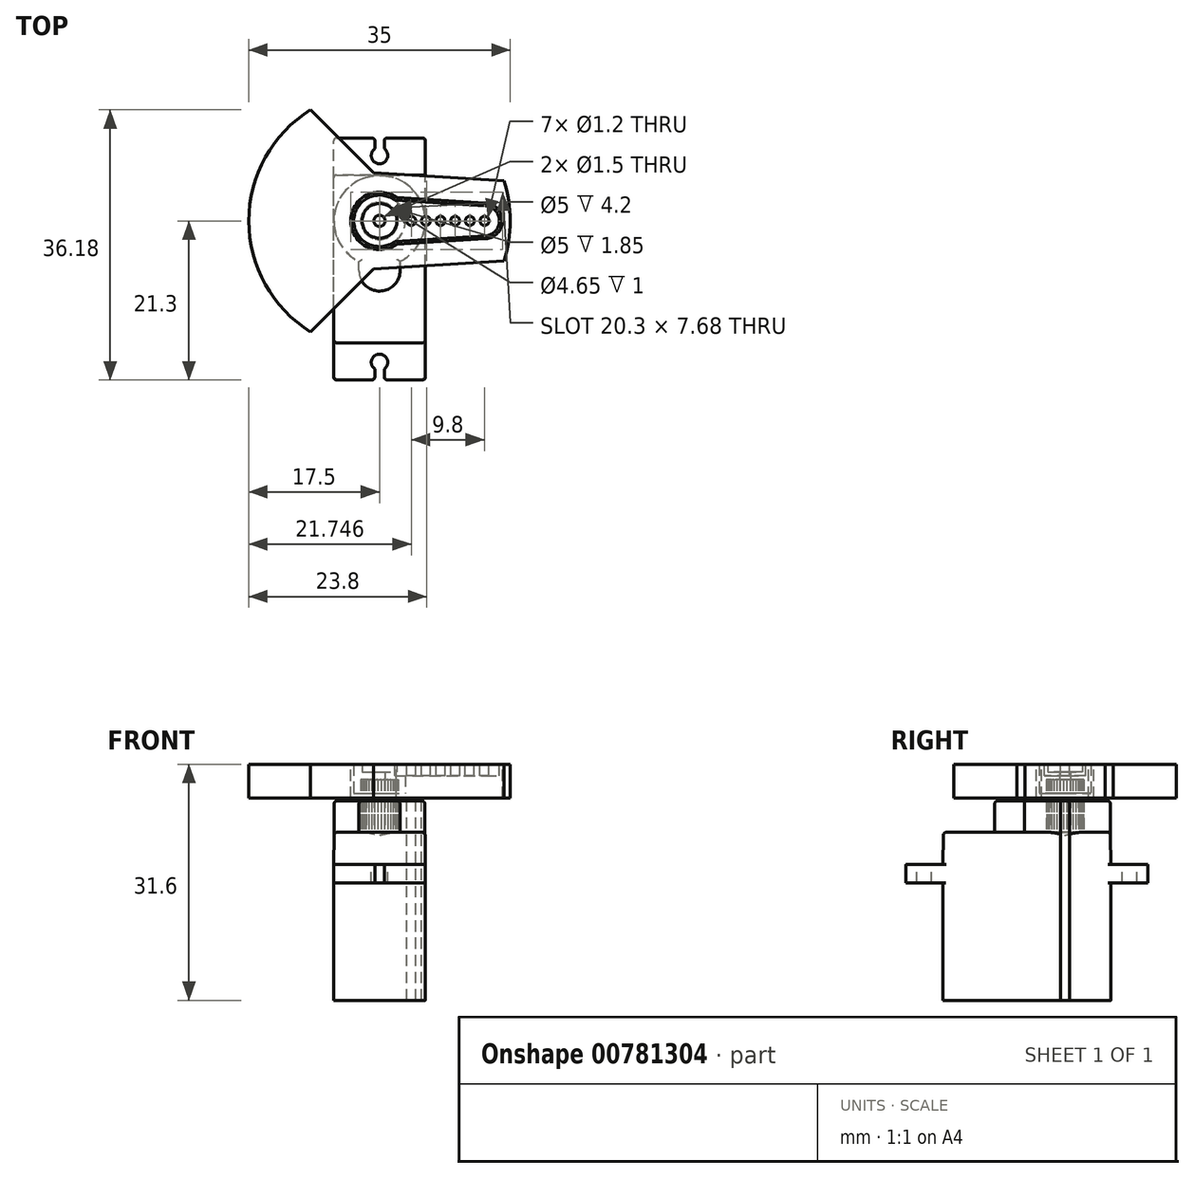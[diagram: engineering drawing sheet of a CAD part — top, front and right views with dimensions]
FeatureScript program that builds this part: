
annotation { "Feature Type Name" : "Feature", "Feature Type Description" : "" }
export const myFeature = defineFeature(function(context is Context, id is Id, definition is map)
    precondition{}
    {
        {
            var Q0;
            Q0=qCreatedBy(makeId("Top.planeOp"),FACE);
            var sketch = newSketch(context, id + "F0", { "sketchPlane" : qUnion([Q0])});
            skLineSegment(sketch, "E0.bottom", {"start": v(6.15, -11.25) * mm, "end": v(-6.15, -11.25) * mm});
            skLineSegment(sketch, "E0.top", {"start": v(6.15, 11.25) * mm, "end": v(-6.15, 11.25) * mm});
            skLineSegment(sketch, "E0.left", {"start": v(6.15, -11.25) * mm, "end": v(6.15, 11.25) * mm});
            skLineSegment(sketch, "E0.right", {"start": v(-6.15, -11.25) * mm, "end": v(-6.15, 11.25) * mm});
            skPoint(sketch, "E0.middle", {"position": v(0, 0) * mm});
            skSolve(sketch);
        }
        {
            var Q0;
            Q0=qSketchRegion(id+"F0",true);
            extrude(context, id + "F1", {"entities" : qUnion([Q0]), "depth" : (22.5 - 15.7) * mm, "hasDraft" : true, "draftAngle" : .5 * degree, "draftPullDirection" : true, "hasSecondDirection" : true, "secondDirectionOppositeDirection" : true, "secondDirectionDepth" : 15.7 * mm});
        }
        {
            var Q0;
            Q0=qCreatedBy(makeId("Top.planeOp"),FACE);
            var sketch = newSketch(context, id + "F2", { "sketchPlane" : qUnion([Q0])});
            skLineSegment(sketch, "E1.bottom", {"start": v(6.15, -16.2) * mm, "end": v(-6.15, -16.2) * mm});
            skLineSegment(sketch, "E1.top", {"start": v(6.15, 16.2) * mm, "end": v(-6.15, 16.2) * mm});
            skLineSegment(sketch, "E1.left", {"start": v(6.15, -16.2) * mm, "end": v(6.15, 16.2) * mm});
            skLineSegment(sketch, "E1.right", {"start": v(-6.15, -16.2) * mm, "end": v(-6.15, 16.2) * mm});
            skPoint(sketch, "E1.middle", {"position": v(0, 0) * mm});
            skSolve(sketch);
        }
        {
            var Q0;
            Q0=qSketchRegion(id+"F2",true);
            extrude(context, id + "F3", {"entities" : qUnion([Q0]), "operationType" : NewBodyOperationType.ADD, "depth" : 2.5 * mm, "hasDraft" : true, "draftAngle" : .5 * degree, "draftPullDirection" : true});
        }
        {
            var Q0;
            {var subQ0=sQuery(id+"F2.wireOp",EDGE,"E1.top");var subQ1=sQuery(id+"F2.wireOp",EDGE,"E1.right");var subQ2=sQuery(id+"F2.wireOp",EDGE,"E1.left");Q0=makeQuery(id+"F3.boolean.opBoolean","SPLIT",FACE,{"disambiguationData":[TD([makeQuery(id+"F1.opExtrude","SWEPT_FACE",FACE,{"disambiguationData":[OSD([sQuery(id+"F0.wireOp",EDGE,"E0.top")])]})])],"derivedFrom":makeQuery(id+"F3.opExtrude","CAP_FACE",FACE,{"disambiguationData":[OSD([sQuery(id+"F2.wireOp",EDGE,"E1.bottom"),subQ0,subQ2,subQ1])],"isStart":false})});}
            var sketch = newSketch(context, id + "F4", { "sketchPlane" : qUnion([Q0])});
            skArc(sketch, "E2", {"start": v(-0.63, 14.76) * mm, "mid": v(0, 12.75) * mm, "end": v(0.63, 14.76) * mm});
            skLineSegment(sketch, "E3", {"start": v(0, 0) * mm, "end": v(0, 13.85) * mm, "construction": true});
            skLineSegment(sketch, "E4", {"start": v(-0.63, 14.76) * mm, "end": v(-0.63, 16.2) * mm});
            skLineSegment(sketch, "E5", {"start": v(-0.62, 16.2) * mm, "end": v(0.62, 16.2) * mm});
            skLineSegment(sketch, "E6", {"start": v(0.62, 16.2) * mm, "end": v(0.62, 14.76) * mm});
            skLineSegment(sketch, "E7", {"start": v(0, 13.85) * mm, "end": v(0, 16.2) * mm, "construction": true});
            skLineSegment(sketch, "E8.MirrorCS", {"start": v(0.62, -16.2) * mm, "end": v(0.62, -14.76) * mm});
            skLineSegment(sketch, "E9.MirrorCS", {"start": v(-0.62, -16.2) * mm, "end": v(0.62, -16.2) * mm});
            skLineSegment(sketch, "E10.MirrorCS", {"start": v(-0.63, -14.76) * mm, "end": v(-0.63, -16.2) * mm});
            skArc(sketch, "E11.MirrorCS", {"start": v(-0.63, -14.76) * mm, "mid": v(0, -12.75) * mm, "end": v(0.63, -14.76) * mm});
            skSolve(sketch);
        }
        {
            var Q0;
            Q0=qSketchRegion(id+"F4",true);
            extrude(context, id + "F5", {"entities" : qUnion([Q0]), "operationType" : NewBodyOperationType.REMOVE, "endBound" : BoundingType.THROUGH_ALL, "oppositeDirection" : true, "depth" : 25 * mm});
        }
        {
            var Q0;
            Q0=makeQuery(id+"F1.*.split.splitOp","SPLIT",EDGE,{"derivedFrom":makeQuery(id+"F1.opExtrude","SWEPT_EDGE",EDGE,{"disambiguationData":[OSD([sQuery(id+"F0.wireOp",EDGE,"E0.bottom"),sQuery(id+"F0.wireOp",EDGE,"E0.left")])]})});
            var Q1;
            Q1=makeQuery(id+"F1.*.split.splitOp","SPLIT",EDGE,{"derivedFrom":makeQuery(id+"F1.opExtrude","SWEPT_EDGE",EDGE,{"disambiguationData":[OSD([sQuery(id+"F0.wireOp",EDGE,"E0.bottom"),sQuery(id+"F0.wireOp",EDGE,"E0.left")])]}),"isFromBackBody":true});
            var Q2;
            Q2=makeQuery(id+"F1.*.split.splitOp","SPLIT",EDGE,{"derivedFrom":makeQuery(id+"F1.opExtrude","SWEPT_EDGE",EDGE,{"disambiguationData":[OSD([sQuery(id+"F0.wireOp",EDGE,"E0.bottom"),sQuery(id+"F0.wireOp",EDGE,"E0.right")])]}),"isFromBackBody":true});
            var Q3;
            Q3=makeQuery(id+"F1.*.split.splitOp","SPLIT",EDGE,{"derivedFrom":makeQuery(id+"F1.opExtrude","SWEPT_EDGE",EDGE,{"disambiguationData":[OSD([sQuery(id+"F0.wireOp",EDGE,"E0.bottom"),sQuery(id+"F0.wireOp",EDGE,"E0.right")])]})});
            var Q4;
            Q4=makeQuery(id+"F1.opExtrude","CAP_FACE",FACE,{"disambiguationData":[OSD([sQuery(id+"F0.wireOp",EDGE,"E0.bottom"),sQuery(id+"F0.wireOp",EDGE,"E0.top"),sQuery(id+"F0.wireOp",EDGE,"E0.left"),sQuery(id+"F0.wireOp",EDGE,"E0.right")])],"isStart":false});
            var Q5;
            Q5=makeQuery(id+"F1.*.split.splitOp","SPLIT",EDGE,{"derivedFrom":makeQuery(id+"F1.opExtrude","SWEPT_EDGE",EDGE,{"disambiguationData":[OSD([sQuery(id+"F0.wireOp",EDGE,"E0.top"),sQuery(id+"F0.wireOp",EDGE,"E0.right")])]})});
            var Q6;
            Q6=makeQuery(id+"F1.*.split.splitOp","SPLIT",EDGE,{"derivedFrom":makeQuery(id+"F1.opExtrude","SWEPT_EDGE",EDGE,{"disambiguationData":[OSD([sQuery(id+"F0.wireOp",EDGE,"E0.top"),sQuery(id+"F0.wireOp",EDGE,"E0.right")])]}),"isFromBackBody":true});
            var Q7;
            Q7=makeQuery(id+"F1.*.split.splitOp","SPLIT",EDGE,{"derivedFrom":makeQuery(id+"F1.opExtrude","SWEPT_EDGE",EDGE,{"disambiguationData":[OSD([sQuery(id+"F0.wireOp",EDGE,"E0.top"),sQuery(id+"F0.wireOp",EDGE,"E0.left")])]}),"isFromBackBody":true});
            var Q8;
            Q8=makeQuery(id+"F1.*.split.splitOp","SPLIT",EDGE,{"derivedFrom":makeQuery(id+"F1.opExtrude","SWEPT_EDGE",EDGE,{"disambiguationData":[OSD([sQuery(id+"F0.wireOp",EDGE,"E0.top"),sQuery(id+"F0.wireOp",EDGE,"E0.left")])]})});
            var Q9;
            Q9=makeQuery(id+"F3.opExtrude","SWEPT_EDGE",EDGE,{"disambiguationData":[OSD([sQuery(id+"F2.wireOp",EDGE,"E1.top"),sQuery(id+"F2.wireOp",EDGE,"E1.left")])]});
            var Q10;
            Q10=makeQuery(id+"F5.boolean.opBoolean","INTERSECT",EDGE,{"derivedFrom":[makeQuery(id+"F3.opExtrude","SWEPT_FACE",FACE,{"disambiguationData":[OSD([sQuery(id+"F2.wireOp",EDGE,"E1.top")])]}),makeQuery(id+"F5.opExtrude","SWEPT_FACE",FACE,{"disambiguationData":[OSD([sQuery(id+"F4.wireOp",EDGE,"E6")])]})]});
            var Q11;
            Q11=makeQuery(id+"F5.boolean.opBoolean","INTERSECT",EDGE,{"derivedFrom":[makeQuery(id+"F3.opExtrude","SWEPT_FACE",FACE,{"disambiguationData":[OSD([sQuery(id+"F2.wireOp",EDGE,"E1.top")])]}),makeQuery(id+"F5.opExtrude","SWEPT_FACE",FACE,{"disambiguationData":[OSD([sQuery(id+"F4.wireOp",EDGE,"E4")])]})]});
            var Q12;
            Q12=makeQuery(id+"F3.opExtrude","SWEPT_EDGE",EDGE,{"disambiguationData":[OSD([sQuery(id+"F2.wireOp",EDGE,"E1.top"),sQuery(id+"F2.wireOp",EDGE,"E1.right")])]});
            var Q13;
            Q13=makeQuery(id+"F3.opExtrude","SWEPT_EDGE",EDGE,{"disambiguationData":[OSD([sQuery(id+"F2.wireOp",EDGE,"E1.bottom"),sQuery(id+"F2.wireOp",EDGE,"E1.right")])]});
            var Q14;
            Q14=makeQuery(id+"F5.boolean.opBoolean","INTERSECT",EDGE,{"derivedFrom":[makeQuery(id+"F3.opExtrude","SWEPT_FACE",FACE,{"disambiguationData":[OSD([sQuery(id+"F2.wireOp",EDGE,"E1.bottom")])]}),makeQuery(id+"F5.opExtrude","SWEPT_FACE",FACE,{"disambiguationData":[OSD([sQuery(id+"F4.wireOp",EDGE,"E10.MirrorCS")])]})]});
            var Q15;
            Q15=makeQuery(id+"F5.boolean.opBoolean","INTERSECT",EDGE,{"derivedFrom":[makeQuery(id+"F3.opExtrude","SWEPT_FACE",FACE,{"disambiguationData":[OSD([sQuery(id+"F2.wireOp",EDGE,"E1.bottom")])]}),makeQuery(id+"F5.opExtrude","SWEPT_FACE",FACE,{"disambiguationData":[OSD([sQuery(id+"F4.wireOp",EDGE,"E8.MirrorCS")])]})]});
            var Q16;
            Q16=makeQuery(id+"F3.opExtrude","SWEPT_EDGE",EDGE,{"disambiguationData":[OSD([sQuery(id+"F2.wireOp",EDGE,"E1.bottom"),sQuery(id+"F2.wireOp",EDGE,"E1.left")])]});
            fillet(context, id + "F6", {"entities" : qUnion([Q0, Q1, Q2, Q3, Q4, Q5, Q6, Q7, Q8, Q9, Q10, Q11, Q12, Q13, Q14, Q15, Q16]), "radius" : .4 * mm, "tangentPropagation" : true, "allowEdgeOverflow" : false});
        }
        {
            var Q0;
            Q0=makeQuery(id+"F1.opExtrude","CAP_FACE",FACE,{"disambiguationData":[OSD([sQuery(id+"F0.wireOp",EDGE,"E0.bottom"),sQuery(id+"F0.wireOp",EDGE,"E0.top"),sQuery(id+"F0.wireOp",EDGE,"E0.left"),sQuery(id+"F0.wireOp",EDGE,"E0.right")])],"isStart":false});
            var sketch = newSketch(context, id + "F7", { "sketchPlane" : qUnion([Q0])});
            skArc(sketch, "E12", {"start": v(2.75, -0.34) * mm, "mid": v(0, 11.2) * mm, "end": v(-2.75, -0.34) * mm});
            skLineSegment(sketch, "E13", {"start": v(-2.75, -0.34) * mm, "end": v(-2.75, -1.56) * mm});
            skLineSegment(sketch, "E14", {"start": v(2.75, -0.34) * mm, "end": v(2.75, -1.56) * mm});
            skArc(sketch, "E15", {"start": v(-2.75, -1.56) * mm, "mid": v(0, -4.3) * mm, "end": v(2.75, -1.56) * mm});
            skCircle(sketch, "E16", {"center": v(0, 5.1) * mm, "radius": 2.5 * mm});
            skSolve(sketch);
        }
        {
            var Q0;
            Q0=qSketchRegion(id+"F7",true);
            extrude(context, id + "F8", {"entities" : qUnion([Q0]), "operationType" : NewBodyOperationType.ADD, "depth" : 4.2 * mm, "hasSecondDirection" : true, "secondDirectionBound" : SecondDirectionBoundingType.UP_TO_NEXT, "secondDirectionOppositeDirection" : true, "secondDirectionDepth" : 25 * mm});
        }
        {
            var Q0;
            Q0=makeQuery(id+"F8.opExtrude","CAP_EDGE",EDGE,{"disambiguationData":[OSD([sQuery(id+"F7.wireOp",EDGE,"E12")])],"isStart":false});
            var Q1;
            Q1=makeQuery(id+"F8.opExtrude","CAP_EDGE",EDGE,{"disambiguationData":[OSD([sQuery(id+"F7.wireOp",EDGE,"E14")])],"isStart":false});
            var Q2;
            Q2=makeQuery(id+"F8.opExtrude","CAP_EDGE",EDGE,{"disambiguationData":[OSD([sQuery(id+"F7.wireOp",EDGE,"E15")])],"isStart":false});
            var Q3;
            Q3=makeQuery(id+"F8.opExtrude","CAP_EDGE",EDGE,{"disambiguationData":[OSD([sQuery(id+"F7.wireOp",EDGE,"E13")])],"isStart":false});
            fillet(context, id + "F9", {"entities" : qUnion([Q0, Q1, Q2, Q3]), "radius" : .4 * mm, "tangentPropagation" : true, "allowEdgeOverflow" : false});
        }
        {
            var Q0;
            Q0=makeQuery(id+"F8.opExtrude","CAP_FACE",FACE,{"disambiguationData":[OSD([sQuery(id+"F7.wireOp",EDGE,"E12"),sQuery(id+"F7.wireOp",EDGE,"E13"),sQuery(id+"F7.wireOp",EDGE,"E14"),sQuery(id+"F7.wireOp",EDGE,"E15"),sQuery(id+"F7.wireOp",EDGE,"E16")])],"isStart":false});
            var sketch = newSketch(context, id + "F10", { "sketchPlane" : qUnion([Q0])});
            skCircle(sketch, "E17", {"center": v(0, 5.1) * mm, "radius": 2.3 * mm, "construction": true});
            skLineSegment(sketch, "E18", {"start": v(-0.23, 7.39) * mm, "end": v(-0.06, 7.57) * mm});
            skLineSegment(sketch, "E19", {"start": v(0.23, 7.39) * mm, "end": v(0.06, 7.57) * mm});
            skArc(sketch, "E20", {"start": v(0.06, 7.57) * mm, "mid": v(0, 7.6) * mm, "end": v(-0.06, 7.57) * mm});
            skLineSegment(sketch, "E21", {"start": v(-0.23, 7.39) * mm, "end": v(0, 5.1) * mm, "construction": true});
            skLineSegment(sketch, "E22", {"start": v(0.23, 7.39) * mm, "end": v(0, 5.1) * mm, "construction": true});
            skLineSegment(sketch, "E23.1.0", {"start": v(-0.67, 7.3) * mm, "end": v(-0.54, 7.51) * mm});
            skArc(sketch, "E23.1.1", {"start": v(-0.42, 7.54) * mm, "mid": v(-0.49, 7.55) * mm, "end": v(-0.54, 7.51) * mm});
            skLineSegment(sketch, "E23.1.2", {"start": v(-0.23, 7.39) * mm, "end": v(-0.42, 7.54) * mm});
            skLineSegment(sketch, "E23.2.0", {"start": v(-1.08, 7.13) * mm, "end": v(-1, 7.36) * mm});
            skArc(sketch, "E23.2.1", {"start": v(-0.9, 7.4) * mm, "mid": v(-0.96, 7.4) * mm, "end": v(-1, 7.36) * mm});
            skLineSegment(sketch, "E23.2.2", {"start": v(-0.67, 7.3) * mm, "end": v(-0.9, 7.4) * mm});
            skLineSegment(sketch, "E23.3.0", {"start": v(-1.46, 6.88) * mm, "end": v(-1.42, 7.12) * mm});
            skArc(sketch, "E23.3.1", {"start": v(-1.32, 7.19) * mm, "mid": v(-1.39, 7.18) * mm, "end": v(-1.42, 7.12) * mm});
            skLineSegment(sketch, "E23.3.2", {"start": v(-1.08, 7.13) * mm, "end": v(-1.32, 7.19) * mm});
            skLineSegment(sketch, "E23.4.0", {"start": v(-1.78, 6.56) * mm, "end": v(-1.8, 6.8) * mm});
            skArc(sketch, "E23.4.1", {"start": v(-1.7, 6.9) * mm, "mid": v(-1.77, 6.87) * mm, "end": v(-1.8, 6.8) * mm});
            skLineSegment(sketch, "E23.4.2", {"start": v(-1.46, 6.88) * mm, "end": v(-1.7, 6.9) * mm});
            skLineSegment(sketch, "E23.5.0", {"start": v(-2.03, 6.18) * mm, "end": v(-2.09, 6.42) * mm});
            skArc(sketch, "E23.5.1", {"start": v(-2.02, 6.52) * mm, "mid": v(-2.08, 6.49) * mm, "end": v(-2.09, 6.42) * mm});
            skLineSegment(sketch, "E23.5.2", {"start": v(-1.78, 6.56) * mm, "end": v(-2.02, 6.52) * mm});
            skLineSegment(sketch, "E23.6.0", {"start": v(-2.2, 5.77) * mm, "end": v(-2.3, 6) * mm});
            skArc(sketch, "E23.6.1", {"start": v(-2.26, 6.1) * mm, "mid": v(-2.3, 6.06) * mm, "end": v(-2.3, 6) * mm});
            skLineSegment(sketch, "E23.6.2", {"start": v(-2.03, 6.18) * mm, "end": v(-2.26, 6.1) * mm});
            skLineSegment(sketch, "E23.7.0", {"start": v(-2.29, 5.33) * mm, "end": v(-2.44, 5.52) * mm});
            skArc(sketch, "E23.7.1", {"start": v(-2.41, 5.64) * mm, "mid": v(-2.45, 5.59) * mm, "end": v(-2.44, 5.52) * mm});
            skLineSegment(sketch, "E23.7.2", {"start": v(-2.2, 5.77) * mm, "end": v(-2.41, 5.64) * mm});
            skLineSegment(sketch, "E23.8.0", {"start": v(-2.29, 4.87) * mm, "end": v(-2.47, 5.04) * mm});
            skArc(sketch, "E23.8.1", {"start": v(-2.47, 5.16) * mm, "mid": v(-2.5, 5.1) * mm, "end": v(-2.47, 5.04) * mm});
            skLineSegment(sketch, "E23.8.2", {"start": v(-2.29, 5.33) * mm, "end": v(-2.47, 5.16) * mm});
            skLineSegment(sketch, "E23.9.0", {"start": v(-2.2, 4.43) * mm, "end": v(-2.41, 4.56) * mm});
            skArc(sketch, "E23.9.1", {"start": v(-2.44, 4.68) * mm, "mid": v(-2.45, 4.61) * mm, "end": v(-2.41, 4.56) * mm});
            skLineSegment(sketch, "E23.9.2", {"start": v(-2.29, 4.87) * mm, "end": v(-2.44, 4.68) * mm});
            skLineSegment(sketch, "E23.10.0", {"start": v(-2.03, 4.02) * mm, "end": v(-2.26, 4.1) * mm});
            skArc(sketch, "E23.10.1", {"start": v(-2.3, 4.2) * mm, "mid": v(-2.3, 4.14) * mm, "end": v(-2.26, 4.1) * mm});
            skLineSegment(sketch, "E23.10.2", {"start": v(-2.2, 4.43) * mm, "end": v(-2.3, 4.2) * mm});
            skLineSegment(sketch, "E23.11.0", {"start": v(-1.78, 3.64) * mm, "end": v(-2.02, 3.68) * mm});
            skArc(sketch, "E23.11.1", {"start": v(-2.09, 3.78) * mm, "mid": v(-2.08, 3.71) * mm, "end": v(-2.02, 3.68) * mm});
            skLineSegment(sketch, "E23.11.2", {"start": v(-2.03, 4.02) * mm, "end": v(-2.09, 3.78) * mm});
            skLineSegment(sketch, "E23.12.0", {"start": v(-1.46, 3.32) * mm, "end": v(-1.7, 3.3) * mm});
            skArc(sketch, "E23.12.1", {"start": v(-1.8, 3.4) * mm, "mid": v(-1.77, 3.33) * mm, "end": v(-1.7, 3.3) * mm});
            skLineSegment(sketch, "E23.12.2", {"start": v(-1.78, 3.64) * mm, "end": v(-1.8, 3.4) * mm});
            skLineSegment(sketch, "E23.13.0", {"start": v(-1.08, 3.07) * mm, "end": v(-1.32, 3.01) * mm});
            skArc(sketch, "E23.13.1", {"start": v(-1.42, 3.08) * mm, "mid": v(-1.39, 3.02) * mm, "end": v(-1.32, 3.01) * mm});
            skLineSegment(sketch, "E23.13.2", {"start": v(-1.46, 3.32) * mm, "end": v(-1.42, 3.08) * mm});
            skLineSegment(sketch, "E23.14.0", {"start": v(-0.67, 2.9) * mm, "end": v(-0.9, 2.8) * mm});
            skArc(sketch, "E23.14.1", {"start": v(-1, 2.84) * mm, "mid": v(-0.96, 2.8) * mm, "end": v(-0.9, 2.8) * mm});
            skLineSegment(sketch, "E23.14.2", {"start": v(-1.08, 3.07) * mm, "end": v(-1, 2.84) * mm});
            skLineSegment(sketch, "E23.15.0", {"start": v(-0.23, 2.81) * mm, "end": v(-0.42, 2.66) * mm});
            skArc(sketch, "E23.15.1", {"start": v(-0.54, 2.69) * mm, "mid": v(-0.49, 2.65) * mm, "end": v(-0.42, 2.66) * mm});
            skLineSegment(sketch, "E23.15.2", {"start": v(-0.67, 2.9) * mm, "end": v(-0.54, 2.69) * mm});
            skLineSegment(sketch, "E23.16.0", {"start": v(0.23, 2.81) * mm, "end": v(0.06, 2.63) * mm});
            skArc(sketch, "E23.16.1", {"start": v(-0.06, 2.63) * mm, "mid": v(0, 2.6) * mm, "end": v(0.06, 2.63) * mm});
            skLineSegment(sketch, "E23.16.2", {"start": v(-0.23, 2.81) * mm, "end": v(-0.06, 2.63) * mm});
            skLineSegment(sketch, "E23.17.0", {"start": v(0.67, 2.9) * mm, "end": v(0.54, 2.69) * mm});
            skArc(sketch, "E23.17.1", {"start": v(0.42, 2.66) * mm, "mid": v(0.49, 2.65) * mm, "end": v(0.54, 2.69) * mm});
            skLineSegment(sketch, "E23.17.2", {"start": v(0.23, 2.81) * mm, "end": v(0.42, 2.66) * mm});
            skLineSegment(sketch, "E23.18.0", {"start": v(1.08, 3.07) * mm, "end": v(1, 2.84) * mm});
            skArc(sketch, "E23.18.1", {"start": v(0.9, 2.8) * mm, "mid": v(0.96, 2.8) * mm, "end": v(1, 2.84) * mm});
            skLineSegment(sketch, "E23.18.2", {"start": v(0.67, 2.9) * mm, "end": v(0.9, 2.8) * mm});
            skLineSegment(sketch, "E23.19.0", {"start": v(1.46, 3.32) * mm, "end": v(1.42, 3.08) * mm});
            skArc(sketch, "E23.19.1", {"start": v(1.32, 3.01) * mm, "mid": v(1.39, 3.02) * mm, "end": v(1.42, 3.08) * mm});
            skLineSegment(sketch, "E23.19.2", {"start": v(1.08, 3.07) * mm, "end": v(1.32, 3.01) * mm});
            skLineSegment(sketch, "E23.20.0", {"start": v(1.78, 3.64) * mm, "end": v(1.8, 3.4) * mm});
            skArc(sketch, "E23.20.1", {"start": v(1.7, 3.3) * mm, "mid": v(1.77, 3.33) * mm, "end": v(1.8, 3.4) * mm});
            skLineSegment(sketch, "E23.20.2", {"start": v(1.46, 3.32) * mm, "end": v(1.7, 3.3) * mm});
            skLineSegment(sketch, "E23.21.0", {"start": v(2.03, 4.02) * mm, "end": v(2.09, 3.78) * mm});
            skArc(sketch, "E23.21.1", {"start": v(2.02, 3.68) * mm, "mid": v(2.08, 3.71) * mm, "end": v(2.09, 3.78) * mm});
            skLineSegment(sketch, "E23.21.2", {"start": v(1.78, 3.64) * mm, "end": v(2.02, 3.68) * mm});
            skLineSegment(sketch, "E23.22.0", {"start": v(2.2, 4.43) * mm, "end": v(2.3, 4.2) * mm});
            skArc(sketch, "E23.22.1", {"start": v(2.26, 4.1) * mm, "mid": v(2.3, 4.14) * mm, "end": v(2.3, 4.2) * mm});
            skLineSegment(sketch, "E23.22.2", {"start": v(2.03, 4.02) * mm, "end": v(2.26, 4.1) * mm});
            skLineSegment(sketch, "E23.23.0", {"start": v(2.29, 4.87) * mm, "end": v(2.44, 4.68) * mm});
            skArc(sketch, "E23.23.1", {"start": v(2.41, 4.56) * mm, "mid": v(2.45, 4.61) * mm, "end": v(2.44, 4.68) * mm});
            skLineSegment(sketch, "E23.23.2", {"start": v(2.2, 4.43) * mm, "end": v(2.41, 4.56) * mm});
            skLineSegment(sketch, "E23.24.0", {"start": v(2.29, 5.33) * mm, "end": v(2.47, 5.16) * mm});
            skArc(sketch, "E23.24.1", {"start": v(2.47, 5.04) * mm, "mid": v(2.5, 5.1) * mm, "end": v(2.47, 5.16) * mm});
            skLineSegment(sketch, "E23.24.2", {"start": v(2.29, 4.87) * mm, "end": v(2.47, 5.04) * mm});
            skLineSegment(sketch, "E23.25.0", {"start": v(2.2, 5.77) * mm, "end": v(2.41, 5.64) * mm});
            skArc(sketch, "E23.25.1", {"start": v(2.44, 5.52) * mm, "mid": v(2.45, 5.59) * mm, "end": v(2.41, 5.64) * mm});
            skLineSegment(sketch, "E23.25.2", {"start": v(2.29, 5.33) * mm, "end": v(2.44, 5.52) * mm});
            skLineSegment(sketch, "E23.26.0", {"start": v(2.03, 6.18) * mm, "end": v(2.26, 6.1) * mm});
            skArc(sketch, "E23.26.1", {"start": v(2.3, 6) * mm, "mid": v(2.3, 6.06) * mm, "end": v(2.26, 6.1) * mm});
            skLineSegment(sketch, "E23.26.2", {"start": v(2.2, 5.77) * mm, "end": v(2.3, 6) * mm});
            skLineSegment(sketch, "E23.27.0", {"start": v(1.78, 6.56) * mm, "end": v(2.02, 6.52) * mm});
            skArc(sketch, "E23.27.1", {"start": v(2.09, 6.42) * mm, "mid": v(2.08, 6.49) * mm, "end": v(2.02, 6.52) * mm});
            skLineSegment(sketch, "E23.27.2", {"start": v(2.03, 6.18) * mm, "end": v(2.09, 6.42) * mm});
            skLineSegment(sketch, "E23.28.0", {"start": v(1.46, 6.88) * mm, "end": v(1.7, 6.9) * mm});
            skArc(sketch, "E23.28.1", {"start": v(1.8, 6.8) * mm, "mid": v(1.77, 6.87) * mm, "end": v(1.7, 6.9) * mm});
            skLineSegment(sketch, "E23.28.2", {"start": v(1.78, 6.56) * mm, "end": v(1.8, 6.8) * mm});
            skLineSegment(sketch, "E23.29.0", {"start": v(1.08, 7.13) * mm, "end": v(1.32, 7.19) * mm});
            skArc(sketch, "E23.29.1", {"start": v(1.42, 7.12) * mm, "mid": v(1.39, 7.18) * mm, "end": v(1.32, 7.19) * mm});
            skLineSegment(sketch, "E23.29.2", {"start": v(1.46, 6.88) * mm, "end": v(1.42, 7.12) * mm});
            skLineSegment(sketch, "E23.30.0", {"start": v(0.67, 7.3) * mm, "end": v(0.9, 7.4) * mm});
            skArc(sketch, "E23.30.1", {"start": v(1, 7.36) * mm, "mid": v(0.96, 7.4) * mm, "end": v(0.9, 7.4) * mm});
            skLineSegment(sketch, "E23.30.2", {"start": v(1.08, 7.13) * mm, "end": v(1, 7.36) * mm});
            skLineSegment(sketch, "E23.31.0", {"start": v(0.23, 7.39) * mm, "end": v(0.42, 7.54) * mm});
            skArc(sketch, "E23.31.1", {"start": v(0.54, 7.51) * mm, "mid": v(0.49, 7.55) * mm, "end": v(0.42, 7.54) * mm});
            skLineSegment(sketch, "E23.31.2", {"start": v(0.67, 7.3) * mm, "end": v(0.54, 7.51) * mm});
            skCircle(sketch, "E24", {"center": v(0, 5.1) * mm, "radius": 0.75 * mm});
            skSolve(sketch);
        }
        {
            var Q0;
            Q0=qSketchRegion(id+"F10",true);
            extrude(context, id + "F11", {"entities" : qUnion([Q0]), "depth" : 2.85 * mm, "hasSecondDirection" : true, "secondDirectionBound" : SecondDirectionBoundingType.UP_TO_NEXT, "secondDirectionOppositeDirection" : true, "secondDirectionDepth" : 25 * mm, "offsetDistance" : 25 * mm});
        }
        {
            var Q0;
            Q0=qCreatedBy(makeId("Right.planeOp"),FACE);
            var sketch = newSketch(context, id + "F12", { "sketchPlane" : qUnion([Q0])});
            skLineSegment(sketch, "E25.0", {"start": v(4.35, 13.85) * mm, "end": v(5.85, 13.85) * mm, "construction": true});
            skLineSegment(sketch, "E26", {"start": v(5.85, 13.85) * mm, "end": v(7.6, 13.85) * mm});
            skLineSegment(sketch, "E27", {"start": v(7.6, 13.85) * mm, "end": v(7.6, 12) * mm});
            skLineSegment(sketch, "E28", {"start": v(7.6, 12) * mm, "end": v(8.55, 12) * mm});
            skLineSegment(sketch, "E29", {"start": v(8.55, 12) * mm, "end": v(8.55, 15.9) * mm});
            skLineSegment(sketch, "E30", {"start": v(8.55, 15.9) * mm, "end": v(7.43, 15.9) * mm});
            skLineSegment(sketch, "E31", {"start": v(7.43, 15.9) * mm, "end": v(7.43, 14.9) * mm});
            skLineSegment(sketch, "E32", {"start": v(7.43, 14.9) * mm, "end": v(5.85, 14.9) * mm});
            skLineSegment(sketch, "E33", {"start": v(5.85, 14.9) * mm, "end": v(5.85, 13.85) * mm});
            skLineSegment(sketch, "E34", {"start": v(5.1, 13.85) * mm, "end": v(5.1, 16.3) * mm, "construction": true});
            skLineSegment(sketch, "E35.0", {"start": v(2.6, 11) * mm, "end": v(7.6, 11) * mm, "construction": true});
            skSolve(sketch);
        }
        {
            var Q0;
            Q0=qSketchRegion(id+"F12",true);
            var Q1;
            Q1=qSketchRegion(id+"F19",true);
            var Q2;
            Q2=sQuery(id+"F12.wireOp",EDGE,"E34");
            revolve(context, id + "F13", {"entities" : qUnion([Q0, Q1]), "axis" : qUnion([Q2]), "revolveType" : RevolveType.FULL, "surfaceOperationType" : NewSurfaceOperationType.NEW});
        }
        {
            var Q0;
            Q0=makeQuery(id+"F13.opRevolve","SWEPT_FACE",FACE,{"disambiguationData":[OSD([sQuery(id+"F12.wireOp",EDGE,"E30")])]});
            var sketch = newSketch(context, id + "F14", { "sketchPlane" : qUnion([Q0])});
            skLineSegment(sketch, "E36", {"start": v(2.08, 2.35) * mm, "end": v(14.17, 3.1) * mm});
            skLineSegment(sketch, "E37", {"start": v(2.08, 7.85) * mm, "end": v(14.17, 7.1) * mm});
            skLineSegment(sketch, "E38", {"start": v(0, 5.1) * mm, "end": v(14.05, 5.1) * mm, "construction": true});
            skArc(sketch, "E39", {"start": v(14.17, 3.1) * mm, "mid": v(16.05, 5.1) * mm, "end": v(14.17, 7.1) * mm});
            skArc(sketch, "E40.0", {"start": v(2.08, 2.35) * mm, "mid": v(3.45, 5.1) * mm, "end": v(2.08, 7.85) * mm});
            skSolve(sketch);
        }
        {
            var Q0;
            Q0=qSketchRegion(id+"F14",true);
            extrude(context, id + "F15", {"entities" : qUnion([Q0]), "operationType" : NewBodyOperationType.ADD, "oppositeDirection" : true, "depth" : 1.5 * mm, "offsetDistance" : 25 * mm});
        }
        {
            var Q0;
            Q0=makeQuery(id+"F15.boolean.opBoolean","MERGE",FACE,{"derivedFrom":[makeQuery(id+"F13.opRevolve","SWEPT_FACE",FACE,{"disambiguationData":[OSD([sQuery(id+"F12.wireOp",EDGE,"E30")])]}),makeQuery(id+"F15.opExtrude","CAP_FACE",FACE,{"disambiguationData":[OSD([sQuery(id+"F14.wireOp",EDGE,"E36"),sQuery(id+"F14.wireOp",EDGE,"E37"),sQuery(id+"F14.wireOp",EDGE,"E39"),sQuery(id+"F14.wireOp",EDGE,"E40.0")])],"isStart":true})]});
            var sketch = newSketch(context, id + "F16", { "sketchPlane" : qUnion([Q0])});
            skCircle(sketch, "E41", {"center": v(14.05, 5.1) * mm, "radius": 0.6 * mm});
            skCircle(sketch, "E42.1.0.0", {"center": v(12.09, 5.1) * mm, "radius": 0.6 * mm});
            skCircle(sketch, "E42.2.0.0", {"center": v(10.13, 5.1) * mm, "radius": 0.6 * mm});
            skCircle(sketch, "E42.3.0.0", {"center": v(8.17, 5.1) * mm, "radius": 0.6 * mm});
            skCircle(sketch, "E42.4.0.0", {"center": v(6.2, 5.1) * mm, "radius": 0.6 * mm});
            skCircle(sketch, "E42.5.0.0", {"center": v(4.25, 5.1) * mm, "radius": 0.6 * mm});
            skLineSegment(sketch, "E42.direction1", {"start": v(14.05, 5.1) * mm, "end": v(12.09, 5.1) * mm, "construction": true});
            skSolve(sketch);
        }
        {
            var Q0;
            Q0=qSketchRegion(id+"F16",true);
            extrude(context, id + "F17", {"entities" : qUnion([Q0]), "operationType" : NewBodyOperationType.REMOVE, "endBound" : BoundingType.THROUGH_ALL, "oppositeDirection" : true, "depth" : 25 * mm, "offsetDistance" : 25 * mm});
        }
        {
            var Q0;
            Q0=makeQuery(id+"F15.boolean.opBoolean","MERGE",FACE,{"derivedFrom":[makeQuery(id+"F13.opRevolve","SWEPT_FACE",FACE,{"disambiguationData":[OSD([sQuery(id+"F12.wireOp",EDGE,"E30")])]}),makeQuery(id+"F15.opExtrude","CAP_FACE",FACE,{"disambiguationData":[OSD([sQuery(id+"F14.wireOp",EDGE,"E36"),sQuery(id+"F14.wireOp",EDGE,"E37"),sQuery(id+"F14.wireOp",EDGE,"E39"),sQuery(id+"F14.wireOp",EDGE,"E40.0")])],"isStart":true})]});
            var sketch = newSketch(context, id + "F18", { "sketchPlane" : qUnion([Q0])});
            skArc(sketch, "E43.0", {"start": v(2.22, 8.24) * mm, "mid": v(-3.85, 5.1) * mm, "end": v(2.22, 1.96) * mm});
            skLineSegment(sketch, "E43.1", {"start": v(14.2, 7.5) * mm, "end": v(2.22, 8.24) * mm});
            skArc(sketch, "E43.2", {"start": v(14.2, 2.7) * mm, "mid": v(16.45, 5.1) * mm, "end": v(14.2, 7.5) * mm});
            skLineSegment(sketch, "E43.3", {"start": v(2.22, 1.96) * mm, "end": v(14.2, 2.7) * mm});
            skSolve(sketch);
        }
        {
            var Q0;
            Q0=makeQuery(id+"F18.imprint","IMPRINT",FACE,{"disambiguationData":[TD([[makeQuery(id+"F18.imprint","IMPRINT",EDGE,{"derivedFrom":sQuery(id+"F18.wireOp",EDGE,"E43.0")}),1.0]])]});
            var sketch = newSketch(context, id + "F19", { "sketchPlane" : qUnion([Q0])});
            skCircle(sketch, "E44", {"center": v(0, 5.1) * mm, "radius": 17.5 * mm});
            skLineSegment(sketch, "E45", {"start": v(0, 5.1) * mm, "end": v(-14.14, -9.04) * mm});
            skLineSegment(sketch, "E46", {"start": v(0, 5.1) * mm, "end": v(-20.07, 5.1) * mm});
            skLineSegment(sketch, "E47.MirrorCS", {"start": v(0, 5.1) * mm, "end": v(-14.14, 19.24) * mm});
            skCircle(sketch, "E48", {"center": v(-14, 5.1) * mm, "radius": 2 * mm});
            skCircle(sketch, "E49", {"center": v(0, 5.1) * mm, "radius": 14 * mm});
            skCircle(sketch, "E50.1.0", {"center": v(-12.93, 10.46) * mm, "radius": 2 * mm});
            skCircle(sketch, "E50.2.0", {"center": v(-9.9, 15) * mm, "radius": 2 * mm});
            skLineSegment(sketch, "E50.anchor1", {"start": v(0, 5.1) * mm, "end": v(-14, 5.1) * mm, "construction": true});
            skLineSegment(sketch, "E50.anchor2", {"start": v(0, 5.1) * mm, "end": v(-9.9, 15) * mm, "construction": true});
            skCircle(sketch, "E51.MirrorC", {"center": v(-12.93, -0.26) * mm, "radius": 2 * mm});
            skCircle(sketch, "E52.MirrorC", {"center": v(-9.9, -4.8) * mm, "radius": 2 * mm});
            skLineSegment(sketch, "E53.0", {"start": v(5.66, 5.1) * mm, "end": v(-11.31, 22.07) * mm});
            skLineSegment(sketch, "E53.1", {"start": v(5.66, 5.1) * mm, "end": v(-11.31, -11.87) * mm});
            skLineSegment(sketch, "E54", {"start": v(0, 5.1) * mm, "end": v(-12.93, -0.26) * mm});
            skLineSegment(sketch, "E55", {"start": v(0, 5.1) * mm, "end": v(-12.93, 10.46) * mm});
            skLineSegment(sketch, "E56", {"start": v(-12.04, 12.25) * mm, "end": v(19.23, 10.3) * mm});
            skLineSegment(sketch, "E57.MirrorCS", {"start": v(-12.04, -2.05) * mm, "end": v(19.23, -0.1) * mm});
            skSolve(sketch);
        }
        {
            var Q0;
            {var subQ5=sQuery(id+"F19.wireOp",EDGE,"E53.0");var subQ7=sQuery(id+"F19.wireOp",EDGE,"E44");var subQ8=makeQuery(id+"F19.imprint","INTERSECT",VERTEX,{"derivedFrom":[subQ7,subQ5]});Q0=makeQuery(id+"F19.imprint","IMPRINT",FACE,{"disambiguationData":[TD([[makeQuery(id+"F19.imprint","IMPRINT",EDGE,{"disambiguationData":[TD([[subQ8,-1.0]])],"derivedFrom":subQ7}),1.0]])]});}
            var Q1;
            {var subQ3=sQuery(id+"F19.wireOp",EDGE,"E56");var subQ6=sQuery(id+"F19.wireOp",EDGE,"E47.MirrorCS");var subQ9=makeQuery(id+"F19.imprint","INTERSECT",VERTEX,{"derivedFrom":[subQ6,subQ3]});Q1=makeQuery(id+"F19.imprint","IMPRINT",FACE,{"disambiguationData":[TD([[makeQuery(id+"F19.imprint","IMPRINT",EDGE,{"disambiguationData":[TD([[subQ9,-1.0]])],"derivedFrom":subQ6}),-1.0]])]});}
            var Q2;
            {var subQ3=sQuery(id+"F19.wireOp",EDGE,"E47.MirrorCS");var subQ5=sQuery(id+"F19.wireOp",EDGE,"E56");var subQ9=makeQuery(id+"F19.imprint","INTERSECT",VERTEX,{"derivedFrom":[subQ3,subQ5]});Q2=makeQuery(id+"F19.imprint","IMPRINT",FACE,{"disambiguationData":[TD([[makeQuery(id+"F19.imprint","IMPRINT",EDGE,{"disambiguationData":[TD([[subQ9,1.0]])],"derivedFrom":subQ3}),-1.0]])]});}
            var Q3;
            {var subQ0=sQuery(id+"F19.wireOp",EDGE,"E56");var subQ1=sQuery(id+"F19.wireOp",EDGE,"E49");var subQ2=makeQuery(id+"F19.imprint","INTERSECT",VERTEX,{"derivedFrom":[subQ1,subQ0]});Q3=makeQuery(id+"F19.imprint","IMPRINT",FACE,{"disambiguationData":[TD([[makeQuery(id+"F19.imprint","IMPRINT",EDGE,{"disambiguationData":[TD([[subQ2,1.0]])],"derivedFrom":subQ1}),1.0]])]});}
            var Q4;
            {var subQ12=makeQuery(id+"F18.imprint","IMPRINT",EDGE,{"derivedFrom":sQuery(id+"F18.wireOp",EDGE,"E43.2")});Q4=makeQuery(id+"F19.imprint","IMPRINT",FACE,{"disambiguationData":[TD([[makeQuery(id+"F19.imprint","IMPRINT",EDGE,{"derivedFrom":subQ12}),-1.0]])]});}
            var Q5;
            {var subQ0=sQuery(id+"F19.wireOp",EDGE,"E57.MirrorCS");var subQ1=sQuery(id+"F19.wireOp",EDGE,"E49");var subQ2=makeQuery(id+"F19.imprint","INTERSECT",VERTEX,{"derivedFrom":[subQ1,subQ0]});Q5=makeQuery(id+"F19.imprint","IMPRINT",FACE,{"disambiguationData":[TD([[makeQuery(id+"F19.imprint","IMPRINT",EDGE,{"disambiguationData":[TD([[subQ2,-1.0]])],"derivedFrom":subQ1}),1.0]])]});}
            var Q6;
            {var subQ3=sQuery(id+"F19.wireOp",EDGE,"E45");var subQ5=sQuery(id+"F19.wireOp",EDGE,"E57.MirrorCS");var subQ9=makeQuery(id+"F19.imprint","INTERSECT",VERTEX,{"derivedFrom":[subQ3,subQ5]});Q6=makeQuery(id+"F19.imprint","IMPRINT",FACE,{"disambiguationData":[TD([[makeQuery(id+"F19.imprint","IMPRINT",EDGE,{"disambiguationData":[TD([[subQ9,1.0]])],"derivedFrom":subQ3}),1.0]])]});}
            var Q7;
            {var subQ0=sQuery(id+"F19.wireOp",EDGE,"E57.MirrorCS");var subQ3=sQuery(id+"F19.wireOp",EDGE,"E45");var subQ4=makeQuery(id+"F19.imprint","INTERSECT",VERTEX,{"derivedFrom":[subQ3,subQ0]});Q7=makeQuery(id+"F19.imprint","IMPRINT",FACE,{"disambiguationData":[TD([[makeQuery(id+"F19.imprint","IMPRINT",EDGE,{"disambiguationData":[TD([[subQ4,1.0]])],"derivedFrom":subQ3}),-1.0]])]});}
            var Q8;
            {var subQ0=sQuery(id+"F19.wireOp",EDGE,"E56");var subQ3=sQuery(id+"F19.wireOp",EDGE,"E47.MirrorCS");var subQ4=makeQuery(id+"F19.imprint","INTERSECT",VERTEX,{"derivedFrom":[subQ3,subQ0]});Q8=makeQuery(id+"F19.imprint","IMPRINT",FACE,{"disambiguationData":[TD([[makeQuery(id+"F19.imprint","IMPRINT",EDGE,{"disambiguationData":[TD([[subQ4,1.0]])],"derivedFrom":subQ3}),1.0]])]});}
            var Q9;
            {var subQ1=sQuery(id+"F19.wireOp",EDGE,"E48");var subQ9=sQuery(id+"F19.wireOp",EDGE,"E46");var subQ10=makeQuery(id+"F19.imprint","INTERSECT",VERTEX,{"disambiguationData":[OD(0.0)],"derivedFrom":[subQ9,subQ1]});Q9=makeQuery(id+"F19.imprint","IMPRINT",FACE,{"disambiguationData":[TD([[makeQuery(id+"F19.imprint","IMPRINT",EDGE,{"disambiguationData":[TD([[subQ10,1.0]])],"derivedFrom":subQ9}),-1.0]])]});}
            var Q10;
            {var subQ5=sQuery(id+"F19.wireOp",EDGE,"E48");var subQ6=sQuery(id+"F19.wireOp",EDGE,"E46");var subQ7=makeQuery(id+"F19.imprint","INTERSECT",VERTEX,{"disambiguationData":[OD(0.0)],"derivedFrom":[subQ6,subQ5]});Q10=makeQuery(id+"F19.imprint","IMPRINT",FACE,{"disambiguationData":[TD([[makeQuery(id+"F19.imprint","IMPRINT",EDGE,{"disambiguationData":[TD([[subQ7,1.0]])],"derivedFrom":subQ6}),1.0]])]});}
            var Q11;
            {var subQ3=sQuery(id+"F19.wireOp",EDGE,"E57.MirrorCS");var subQ5=sQuery(id+"F19.wireOp",EDGE,"E45");var subQ6=makeQuery(id+"F19.imprint","INTERSECT",VERTEX,{"derivedFrom":[subQ5,subQ3]});Q11=makeQuery(id+"F19.imprint","IMPRINT",FACE,{"disambiguationData":[TD([[makeQuery(id+"F19.imprint","IMPRINT",EDGE,{"disambiguationData":[TD([[subQ6,-1.0]])],"derivedFrom":subQ5}),1.0]])]});}
            var Q12;
            {var subQ0=sQuery(id+"F19.wireOp",EDGE,"E57.MirrorCS");var subQ1=sQuery(id+"F19.wireOp",EDGE,"E45");var subQ2=makeQuery(id+"F19.imprint","INTERSECT",VERTEX,{"derivedFrom":[subQ1,subQ0]});Q12=makeQuery(id+"F19.imprint","IMPRINT",FACE,{"disambiguationData":[TD([[makeQuery(id+"F19.imprint","IMPRINT",EDGE,{"disambiguationData":[TD([[subQ2,-1.0]])],"derivedFrom":subQ1}),-1.0]])]});}
            var Q13;
            {var subQ0=sQuery(id+"F19.wireOp",EDGE,"E56");var subQ1=sQuery(id+"F19.wireOp",EDGE,"E47.MirrorCS");var subQ2=makeQuery(id+"F19.imprint","INTERSECT",VERTEX,{"derivedFrom":[subQ1,subQ0]});Q13=makeQuery(id+"F19.imprint","IMPRINT",FACE,{"disambiguationData":[TD([[makeQuery(id+"F19.imprint","IMPRINT",EDGE,{"disambiguationData":[TD([[subQ2,-1.0]])],"derivedFrom":subQ1}),1.0]])]});}
            var Q14;
            {var subQ5=sQuery(id+"F19.wireOp",EDGE,"E47.MirrorCS");var subQ6=sQuery(id+"F19.wireOp",EDGE,"E44");var subQ7=makeQuery(id+"F19.imprint","INTERSECT",VERTEX,{"derivedFrom":[subQ6,subQ5]});Q14=makeQuery(id+"F19.imprint","IMPRINT",FACE,{"disambiguationData":[TD([[makeQuery(id+"F19.imprint","IMPRINT",EDGE,{"disambiguationData":[TD([[subQ7,-1.0]])],"derivedFrom":subQ6}),1.0]])]});}
            var Q15;
            {var subQ1=sQuery(id+"F19.wireOp",EDGE,"E46");var subQ8=sQuery(id+"F19.wireOp",EDGE,"E44");var subQ9=makeQuery(id+"F19.imprint","INTERSECT",VERTEX,{"derivedFrom":[subQ8,subQ1]});Q15=makeQuery(id+"F19.imprint","IMPRINT",FACE,{"disambiguationData":[TD([[makeQuery(id+"F19.imprint","IMPRINT",EDGE,{"disambiguationData":[TD([[subQ9,-1.0]])],"derivedFrom":subQ8}),1.0]])]});}
            var Q16;
            {var subQ1=sQuery(id+"F19.wireOp",EDGE,"E45");var subQ5=sQuery(id+"F19.wireOp",EDGE,"E44");var subQ6=makeQuery(id+"F19.imprint","INTERSECT",VERTEX,{"derivedFrom":[subQ5,subQ1]});Q16=makeQuery(id+"F19.imprint","IMPRINT",FACE,{"disambiguationData":[TD([[makeQuery(id+"F19.imprint","IMPRINT",EDGE,{"disambiguationData":[TD([[subQ6,-1.0]])],"derivedFrom":subQ5}),1.0]])]});}
            var Q17;
            {var subQ0=sQuery(id+"F19.wireOp",EDGE,"E49");var subQ1=sQuery(id+"F19.wireOp",EDGE,"E47.MirrorCS");var subQ2=makeQuery(id+"F19.imprint","INTERSECT",VERTEX,{"derivedFrom":[subQ1,subQ0]});Q17=makeQuery(id+"F19.imprint","IMPRINT",FACE,{"disambiguationData":[TD([[makeQuery(id+"F19.imprint","IMPRINT",EDGE,{"disambiguationData":[TD([[subQ2,-1.0]])],"derivedFrom":subQ1}),-1.0]])]});}
            var Q18;
            {var subQ0=sQuery(id+"F19.wireOp",EDGE,"E49");var subQ1=sQuery(id+"F19.wireOp",EDGE,"E47.MirrorCS");var subQ2=makeQuery(id+"F19.imprint","INTERSECT",VERTEX,{"derivedFrom":[subQ1,subQ0]});Q18=makeQuery(id+"F19.imprint","IMPRINT",FACE,{"disambiguationData":[TD([[makeQuery(id+"F19.imprint","IMPRINT",EDGE,{"disambiguationData":[TD([[subQ2,-1.0]])],"derivedFrom":subQ1}),1.0]])]});}
            var Q19;
            {var subQ0=sQuery(id+"F19.wireOp",EDGE,"E50.2.0");var subQ1=sQuery(id+"F19.wireOp",EDGE,"E47.MirrorCS");var subQ2=makeQuery(id+"F19.imprint","INTERSECT",VERTEX,{"disambiguationData":[OD(0.0)],"derivedFrom":[subQ1,subQ0]});Q19=makeQuery(id+"F19.imprint","IMPRINT",FACE,{"disambiguationData":[TD([[makeQuery(id+"F19.imprint","IMPRINT",EDGE,{"disambiguationData":[TD([[subQ2,-1.0]])],"derivedFrom":subQ1}),1.0]])]});}
            var Q20;
            {var subQ0=sQuery(id+"F19.wireOp",EDGE,"E50.2.0");var subQ1=sQuery(id+"F19.wireOp",EDGE,"E47.MirrorCS");var subQ2=makeQuery(id+"F19.imprint","INTERSECT",VERTEX,{"disambiguationData":[OD(0.0)],"derivedFrom":[subQ1,subQ0]});Q20=makeQuery(id+"F19.imprint","IMPRINT",FACE,{"disambiguationData":[TD([[makeQuery(id+"F19.imprint","IMPRINT",EDGE,{"disambiguationData":[TD([[subQ2,-1.0]])],"derivedFrom":subQ1}),-1.0]])]});}
            var Q21;
            {var subQ0=sQuery(id+"F19.wireOp",EDGE,"E49");var subQ1=makeQuery(id+"F19.imprint","INTERSECT",VERTEX,{"derivedFrom":[subQ0,sQuery(id+"F19.wireOp",EDGE,"E55")]});Q21=makeQuery(id+"F19.imprint","IMPRINT",FACE,{"disambiguationData":[TD([[makeQuery(id+"F19.imprint","IMPRINT",EDGE,{"disambiguationData":[TD([[subQ1,-1.0]])],"derivedFrom":subQ0}),-1.0]])]});}
            var Q22;
            {var subQ0=sQuery(id+"F19.wireOp",EDGE,"E55");var subQ1=sQuery(id+"F19.wireOp",EDGE,"E49");var subQ2=makeQuery(id+"F19.imprint","INTERSECT",VERTEX,{"derivedFrom":[subQ1,subQ0]});Q22=makeQuery(id+"F19.imprint","IMPRINT",FACE,{"disambiguationData":[TD([[makeQuery(id+"F19.imprint","IMPRINT",EDGE,{"disambiguationData":[TD([[subQ2,1.0]])],"derivedFrom":subQ0}),-1.0]])]});}
            var Q23;
            {var subQ0=sQuery(id+"F19.wireOp",EDGE,"E55");var subQ1=sQuery(id+"F19.wireOp",EDGE,"E49");var subQ2=makeQuery(id+"F19.imprint","INTERSECT",VERTEX,{"derivedFrom":[subQ1,subQ0]});Q23=makeQuery(id+"F19.imprint","IMPRINT",FACE,{"disambiguationData":[TD([[makeQuery(id+"F19.imprint","IMPRINT",EDGE,{"disambiguationData":[TD([[subQ2,-1.0]])],"derivedFrom":subQ1}),1.0]])]});}
            var Q24;
            {var subQ0=sQuery(id+"F19.wireOp",EDGE,"E49");var subQ1=sQuery(id+"F19.wireOp",EDGE,"E46");var subQ2=makeQuery(id+"F19.imprint","INTERSECT",VERTEX,{"derivedFrom":[subQ1,subQ0]});Q24=makeQuery(id+"F19.imprint","IMPRINT",FACE,{"disambiguationData":[TD([[makeQuery(id+"F19.imprint","IMPRINT",EDGE,{"disambiguationData":[TD([[subQ2,-1.0]])],"derivedFrom":subQ1}),-1.0]])]});}
            var Q25;
            {var subQ0=sQuery(id+"F19.wireOp",EDGE,"E48");var subQ1=sQuery(id+"F19.wireOp",EDGE,"E46");var subQ2=makeQuery(id+"F19.imprint","INTERSECT",VERTEX,{"disambiguationData":[OD(0.0)],"derivedFrom":[subQ1,subQ0]});Q25=makeQuery(id+"F19.imprint","IMPRINT",FACE,{"disambiguationData":[TD([[makeQuery(id+"F19.imprint","IMPRINT",EDGE,{"disambiguationData":[TD([[subQ2,-1.0]])],"derivedFrom":subQ1}),-1.0]])]});}
            var Q26;
            {var subQ0=sQuery(id+"F19.wireOp",EDGE,"E48");var subQ1=sQuery(id+"F19.wireOp",EDGE,"E46");var subQ2=makeQuery(id+"F19.imprint","INTERSECT",VERTEX,{"disambiguationData":[OD(0.0)],"derivedFrom":[subQ1,subQ0]});Q26=makeQuery(id+"F19.imprint","IMPRINT",FACE,{"disambiguationData":[TD([[makeQuery(id+"F19.imprint","IMPRINT",EDGE,{"disambiguationData":[TD([[subQ2,-1.0]])],"derivedFrom":subQ1}),1.0]])]});}
            var Q27;
            {var subQ0=sQuery(id+"F19.wireOp",EDGE,"E49");var subQ1=sQuery(id+"F19.wireOp",EDGE,"E46");var subQ2=makeQuery(id+"F19.imprint","INTERSECT",VERTEX,{"derivedFrom":[subQ1,subQ0]});Q27=makeQuery(id+"F19.imprint","IMPRINT",FACE,{"disambiguationData":[TD([[makeQuery(id+"F19.imprint","IMPRINT",EDGE,{"disambiguationData":[TD([[subQ2,-1.0]])],"derivedFrom":subQ1}),1.0]])]});}
            var Q28;
            {var subQ0=sQuery(id+"F19.wireOp",EDGE,"E49");var subQ1=makeQuery(id+"F19.imprint","INTERSECT",VERTEX,{"derivedFrom":[subQ0,sQuery(id+"F19.wireOp",EDGE,"E54")]});Q28=makeQuery(id+"F19.imprint","IMPRINT",FACE,{"disambiguationData":[TD([[makeQuery(id+"F19.imprint","IMPRINT",EDGE,{"disambiguationData":[TD([[subQ1,1.0]])],"derivedFrom":subQ0}),-1.0]])]});}
            var Q29;
            {var subQ0=sQuery(id+"F19.wireOp",EDGE,"E54");var subQ1=sQuery(id+"F19.wireOp",EDGE,"E49");var subQ2=makeQuery(id+"F19.imprint","INTERSECT",VERTEX,{"derivedFrom":[subQ1,subQ0]});Q29=makeQuery(id+"F19.imprint","IMPRINT",FACE,{"disambiguationData":[TD([[makeQuery(id+"F19.imprint","IMPRINT",EDGE,{"disambiguationData":[TD([[subQ2,1.0]])],"derivedFrom":subQ1}),1.0]])]});}
            var Q30;
            {var subQ0=sQuery(id+"F19.wireOp",EDGE,"E54");var subQ1=sQuery(id+"F19.wireOp",EDGE,"E49");var subQ2=makeQuery(id+"F19.imprint","INTERSECT",VERTEX,{"derivedFrom":[subQ1,subQ0]});Q30=makeQuery(id+"F19.imprint","IMPRINT",FACE,{"disambiguationData":[TD([[makeQuery(id+"F19.imprint","IMPRINT",EDGE,{"disambiguationData":[TD([[subQ2,1.0]])],"derivedFrom":subQ0}),1.0]])]});}
            var Q31;
            {var subQ0=sQuery(id+"F19.wireOp",EDGE,"E49");var subQ1=sQuery(id+"F19.wireOp",EDGE,"E45");var subQ2=makeQuery(id+"F19.imprint","INTERSECT",VERTEX,{"derivedFrom":[subQ1,subQ0]});Q31=makeQuery(id+"F19.imprint","IMPRINT",FACE,{"disambiguationData":[TD([[makeQuery(id+"F19.imprint","IMPRINT",EDGE,{"disambiguationData":[TD([[subQ2,-1.0]])],"derivedFrom":subQ1}),-1.0]])]});}
            var Q32;
            {var subQ0=sQuery(id+"F19.wireOp",EDGE,"E49");var subQ1=sQuery(id+"F19.wireOp",EDGE,"E45");var subQ2=makeQuery(id+"F19.imprint","INTERSECT",VERTEX,{"derivedFrom":[subQ1,subQ0]});Q32=makeQuery(id+"F19.imprint","IMPRINT",FACE,{"disambiguationData":[TD([[makeQuery(id+"F19.imprint","IMPRINT",EDGE,{"disambiguationData":[TD([[subQ2,-1.0]])],"derivedFrom":subQ1}),1.0]])]});}
            var Q33;
            {var subQ0=sQuery(id+"F19.wireOp",EDGE,"E52.MirrorC");var subQ1=sQuery(id+"F19.wireOp",EDGE,"E45");var subQ2=makeQuery(id+"F19.imprint","INTERSECT",VERTEX,{"disambiguationData":[OD(0.0)],"derivedFrom":[subQ1,subQ0]});Q33=makeQuery(id+"F19.imprint","IMPRINT",FACE,{"disambiguationData":[TD([[makeQuery(id+"F19.imprint","IMPRINT",EDGE,{"disambiguationData":[TD([[subQ2,-1.0]])],"derivedFrom":subQ1}),-1.0]])]});}
            var Q34;
            {var subQ0=sQuery(id+"F19.wireOp",EDGE,"E52.MirrorC");var subQ1=sQuery(id+"F19.wireOp",EDGE,"E45");var subQ2=makeQuery(id+"F19.imprint","INTERSECT",VERTEX,{"disambiguationData":[OD(0.0)],"derivedFrom":[subQ1,subQ0]});Q34=makeQuery(id+"F19.imprint","IMPRINT",FACE,{"disambiguationData":[TD([[makeQuery(id+"F19.imprint","IMPRINT",EDGE,{"disambiguationData":[TD([[subQ2,-1.0]])],"derivedFrom":subQ1}),1.0]])]});}
            extrude(context, id + "F20", {"entities" : qUnion([Q0, Q1, Q2, Q3, Q4, Q5, Q6, Q7, Q8, Q9, Q10, Q11, Q12, Q13, Q14, Q15, Q16, Q17, Q18, Q19, Q20, Q21, Q22, Q23, Q24, Q25, Q26, Q27, Q28, Q29, Q30, Q31, Q32, Q33, Q34]), "oppositeDirection" : true, "depth" : 4.5 * mm, "offsetDistance" : 25 * mm});
        }
    });
